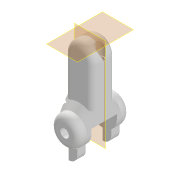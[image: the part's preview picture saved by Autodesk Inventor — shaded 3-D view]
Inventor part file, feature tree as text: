
AUTODESK INVENTOR PART (.ipt)
format: ipt  version: 2020.2 (Build 242310000, 310)  size: 274,432 bytes
history: native  units: mm
features: sketch x9, extrude x6, plane x2, mirror x2, fillet x2, chamfer x1, sweep x1
ambient origin geometry x8: Origin, YZ Plane, XZ Plane, XY Plane, X Axis, Y Axis, Z Axis, Center Point
bodies: Solid1 (feature_tree)
feature tree (23):
  extrude  "base"  Depth=10.0mm
  extrude  "joint"  Depth=20.0mm
  plane  "Work Plane1"
  mirror  "Mirror1"
  chamfer  "Chamfer1"  Distance=8.0mm
  fillet  "Fillet1"  Radius=3.0mm
  extrude  "joint_2"  Depth=5.0mm TaperAngle=0.0deg
  extrude  "lock"  Depth=2.0mm
  mirror  "Mirror2"
  fillet  "Fillet2"  Radius=10.5mm
  sweep  "Sweep2"
  extrude  "Extrusion8"  Depth=3.5mm
  plane  "Work Plane3"
  extrude  "Extrusion9"  Depth=2.5mm
  sketch  "Sketch1"  dims[d0=3.0mm d1=10.0mm]
  sketch  "Sketch2"  dims[d2=20.0mm d3=3.0mm]
  sketch  "Sketch3"  dims[d4=10.0mm d5=8.0mm d6=0.0mm d7=3.0mm]
  sketch  "Sketch9"  dims[d8=10.0mm d9=5.0mm d10=0.0mm]
  sketch  "Sketch10"  dims[d11=2.0mm d12=2.0mm d13=45.0deg d14=2.0mm d15=10.5mm]
  sketch  "Sketch11"  dims[d16=9.0mm d17=0.0mm d21=10.0mm]
  sketch  "Sketch12"  dims[d22=5.25mm d42=3.5mm]
  sketch  "Sketch13"  dims[d43=3.5mm d44=2.5mm]
  sketch  "Sketch14"  dims[d46=25.0mm d47=0.0mm d48=6.0mm d49=3.0mm d50=3.0mm d51=3.0mm d52=0.0mm d53=3.0mm d54=3.0mm d55=7.0mm d57=3.0mm d58=2.0mm d59=2.5mm d60=0.0mm d61=0.0mm d62=4.0mm d63=0.0mm d64=3.5mm d65=3.0mm d66=5.0mm d67=0.0mm]
